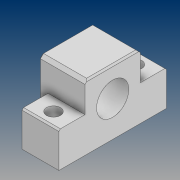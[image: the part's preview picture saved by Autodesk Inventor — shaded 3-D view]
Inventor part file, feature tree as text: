
AUTODESK INVENTOR PART (.ipt)
format: ipt  version: 2021 (Build 250183000, 183)  size: 195,584 bytes
history: native  units: mm
features: chamfer x5, sketch x4, projected_geometry x4, extrude x2, hole x2
ambient origin geometry x8: Origin, YZ Plane, XZ Plane, XY Plane, X Axis, Y Axis, Z Axis, Center Point
bodies: Solid1 (feature_tree)
feature tree (17):
  extrude  "Extrusion1"  Depth=70.0mm
  hole  "Hole1"  [1 undecoded]
  chamfer  "Chamfer1"  Distance=24.0mm
  chamfer  "Chamfer2"  Distance=1.0mm Angle=45.0deg
  chamfer  "Chamfer3"  Distance=1.0mm Angle=45.0deg
  extrude  "Extrusion2"  Depth=2.0mm TaperAngle=45.0deg
  hole  "Hole2"  [1 undecoded]
  chamfer  "Chamfer4"  Distance=5.5mm
  chamfer  "Chamfer5"  Distance=4.0mm
  sketch  "Sketch1"  dims[d0=36.0mm d1=70.0mm]
  sketch  "Sketch2"  dims[d2=19.0mm d3=24.0mm]
  projected_geometry  "Projected Loop1"
  projected_geometry  "Projected Loop2"
  sketch  "Sketch3"  dims[d4=21.0mm d5=24.0mm d6=0.0mm]
  projected_geometry  "Projected Loop3"
  sketch  "Sketch4"  dims[d7=9.0mm d8=6.0mm d9=4.0mm d10=2.0mm d11=90.0deg d12=8.0mm d13=20.594885mm d14=1.0mm d15=2.0mm d16=45.0deg d17=1.0mm d18=2.0mm d19=45.0deg d20=2.0mm d21=2.0mm d22=45.0deg d23=30.0mm d24=5.5mm d25=0.0mm d26=4.0mm d27=4.0mm d28=6.0mm d29=6.0mm d30=2.0mm d31=90.0deg d32=5.5mm d33=20.594885mm d34=2.0mm d35=2.0mm d36=45.0deg d37=0.5mm d38=2.0mm d39=45.0deg]
  projected_geometry  "Projected Loop4"
note: 2 required parameter values undecoded (feature->parameter linkage not recoverable at this tier; creation-order binding heuristic only, values carry confidence <= 0.55)
